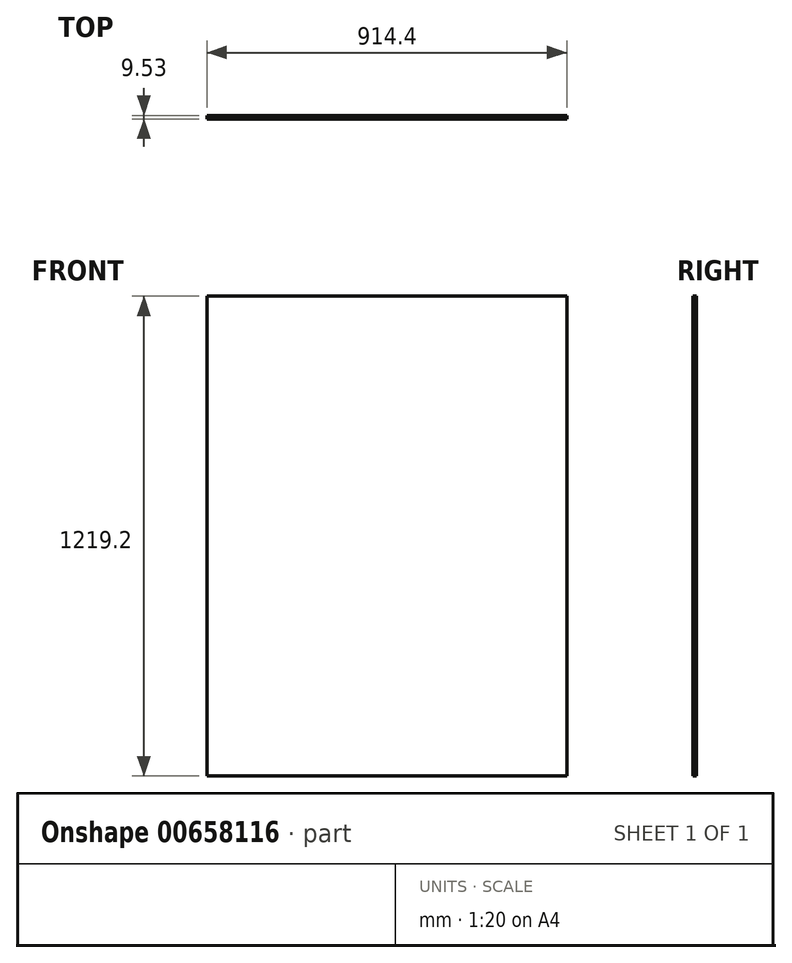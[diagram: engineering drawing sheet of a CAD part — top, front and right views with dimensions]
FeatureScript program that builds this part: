
annotation { "Feature Type Name" : "Feature", "Feature Type Description" : "" }
export const myFeature = defineFeature(function(context is Context, id is Id, definition is map)
    precondition{}
    {
        {
            var Q0;
            Q0=qCreatedBy(makeId("Front.planeOp"),FACE);
            var sketch = newSketch(context, id + "F0", { "sketchPlane" : qUnion([Q0])});
            skLineSegment(sketch, "E0.bottom", {"start": v(457.2, 609.6) * mm, "end": v(-457.2, 609.6) * mm});
            skLineSegment(sketch, "E0.top", {"start": v(457.2, -609.6) * mm, "end": v(-457.2, -609.6) * mm});
            skLineSegment(sketch, "E0.left", {"start": v(457.2, 609.6) * mm, "end": v(457.2, -609.6) * mm});
            skLineSegment(sketch, "E0.right", {"start": v(-457.2, 609.6) * mm, "end": v(-457.2, -609.6) * mm});
            skPoint(sketch, "E0.middle", {"position": v(0, 0) * mm});
            skSolve(sketch);
        }
        {
            var Q0;
            Q0=qSketchRegion(id+"F0",true);
            extrude(context, id + "F1", {"entities" : qUnion([Q0]), "depth" : 9.52 * mm, "offsetDistance" : 25.4 * mm});
        }
    });
